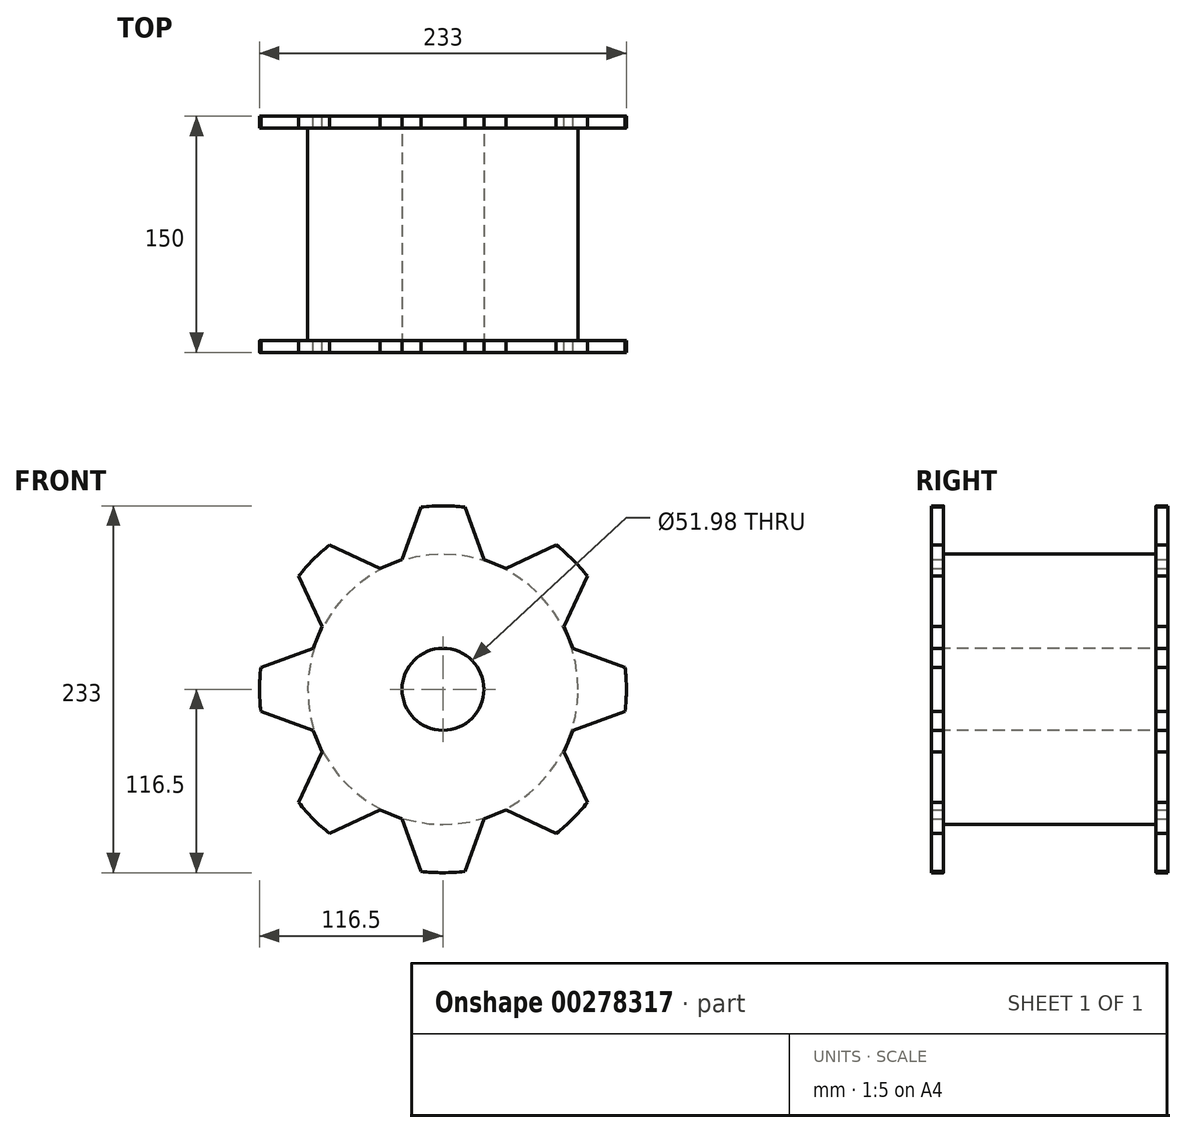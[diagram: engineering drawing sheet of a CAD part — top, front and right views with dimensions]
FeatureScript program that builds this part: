
annotation { "Feature Type Name" : "Feature", "Feature Type Description" : "" }
export const myFeature = defineFeature(function(context is Context, id is Id, definition is map)
    precondition{}
    {
        {
            var Q0;
            Q0=qCreatedBy(makeId("Front.planeOp"),FACE);
            var sketch = newSketch(context, id + "F0", { "sketchPlane" : qUnion([Q0])});
            skLineSegment(sketch, "E0", {"start": v(0, 0) * mm, "end": v(0, 116.5) * mm, "construction": true});
            skLineSegment(sketch, "E1", {"start": v(13.96, 115.66) * mm, "end": v(26.04, 82.49) * mm});
            skLineSegment(sketch, "E2", {"start": v(-13.96, 115.66) * mm, "end": v(-26.04, 82.49) * mm});
            skCircle(sketch, "E3", {"center": v(0, 0) * mm, "radius": 101.5 * mm, "construction": true});
            skArc(sketch, "E4", {"start": v(26.04, 82.49) * mm, "mid": v(0, 86.5) * mm, "end": v(-26.04, 82.49) * mm, "construction": true});
            skArc(sketch, "E5", {"start": v(13.96, 115.66) * mm, "mid": v(0, 116.5) * mm, "end": v(-13.96, 115.66) * mm});
            skPoint(sketch, "E6.startSnap0", {"position": v(-20, 99.07) * mm});
            skLineSegment(sketch, "E7", {"start": v(-20, 99.07) * mm, "end": v(20, 99.07) * mm});
            skArc(sketch, "E8.1.0", {"start": v(-71.91, 91.66) * mm, "mid": v(-82.38, 82.38) * mm, "end": v(-91.66, 71.91) * mm});
            skLineSegment(sketch, "E8.1.1", {"start": v(-71.91, 91.66) * mm, "end": v(-39.92, 76.74) * mm});
            skLineSegment(sketch, "E8.1.2", {"start": v(-91.66, 71.91) * mm, "end": v(-76.74, 39.92) * mm});
            skArc(sketch, "E8.2.0", {"start": v(-115.66, 13.96) * mm, "mid": v(-116.5, 0) * mm, "end": v(-115.66, -13.96) * mm});
            skLineSegment(sketch, "E8.2.1", {"start": v(-115.66, 13.96) * mm, "end": v(-82.49, 26.04) * mm});
            skLineSegment(sketch, "E8.2.2", {"start": v(-115.66, -13.96) * mm, "end": v(-82.49, -26.04) * mm});
            skArc(sketch, "E9.3.3.0", {"start": v(-91.66, -71.91) * mm, "mid": v(-82.38, -82.38) * mm, "end": v(-71.91, -91.66) * mm});
            skLineSegment(sketch, "E9.4.3.0", {"start": v(-91.66, -71.91) * mm, "end": v(-76.74, -39.92) * mm});
            skLineSegment(sketch, "E9.7.3.0", {"start": v(-71.91, -91.66) * mm, "end": v(-39.92, -76.74) * mm});
            skArc(sketch, "E10.3.4.0", {"start": v(-13.96, -115.66) * mm, "mid": v(0, -116.5) * mm, "end": v(13.96, -115.66) * mm});
            skLineSegment(sketch, "E10.4.4.0", {"start": v(-13.96, -115.66) * mm, "end": v(-26.04, -82.49) * mm});
            skLineSegment(sketch, "E10.7.4.0", {"start": v(13.96, -115.66) * mm, "end": v(26.04, -82.49) * mm});
            skArc(sketch, "E10.3.5.0", {"start": v(71.91, -91.66) * mm, "mid": v(82.38, -82.38) * mm, "end": v(91.66, -71.91) * mm});
            skLineSegment(sketch, "E10.4.5.0", {"start": v(71.91, -91.66) * mm, "end": v(39.92, -76.74) * mm});
            skLineSegment(sketch, "E10.7.5.0", {"start": v(91.66, -71.91) * mm, "end": v(76.74, -39.92) * mm});
            skArc(sketch, "E10.3.6.0", {"start": v(115.66, -13.96) * mm, "mid": v(116.5, 0) * mm, "end": v(115.66, 13.96) * mm});
            skLineSegment(sketch, "E10.4.6.0", {"start": v(115.66, -13.96) * mm, "end": v(82.49, -26.04) * mm});
            skLineSegment(sketch, "E10.7.6.0", {"start": v(115.66, 13.96) * mm, "end": v(82.49, 26.04) * mm});
            skArc(sketch, "E10.3.7.0", {"start": v(91.66, 71.91) * mm, "mid": v(82.38, 82.38) * mm, "end": v(71.91, 91.66) * mm});
            skLineSegment(sketch, "E10.4.7.0", {"start": v(91.66, 71.91) * mm, "end": v(76.74, 39.92) * mm});
            skLineSegment(sketch, "E10.7.7.0", {"start": v(71.91, 91.66) * mm, "end": v(39.92, 76.74) * mm});
            skLineSegment(sketch, "E11", {"start": v(-26.04, 82.49) * mm, "end": v(-39.92, 76.74) * mm});
            skLineSegment(sketch, "E12", {"start": v(-76.74, 39.92) * mm, "end": v(-82.49, 26.04) * mm});
            skLineSegment(sketch, "E13", {"start": v(-82.49, -26.04) * mm, "end": v(-76.74, -39.92) * mm});
            skLineSegment(sketch, "E14", {"start": v(-39.92, -76.74) * mm, "end": v(-26.04, -82.49) * mm});
            skLineSegment(sketch, "E15", {"start": v(26.04, -82.49) * mm, "end": v(39.92, -76.74) * mm});
            skLineSegment(sketch, "E16", {"start": v(76.74, -39.92) * mm, "end": v(82.49, -26.04) * mm});
            skLineSegment(sketch, "E17", {"start": v(82.49, 26.04) * mm, "end": v(76.74, 39.92) * mm});
            skLineSegment(sketch, "E18", {"start": v(39.92, 76.74) * mm, "end": v(26.04, 82.49) * mm});
            skSolve(sketch);
        }
        {
            var Q0;
            {var subQ0=sQuery(id+"F0.wireOp",EDGE,"E7");Q0=makeQuery(id+"F0.imprint","IMPRINT",FACE,{"disambiguationData":[TD([[makeQuery(id+"F0.imprint","IMPRINT",EDGE,{"derivedFrom":subQ0}),-1.0]])]});}
            var Q1;
            {var subQ0=sQuery(id+"F0.wireOp",EDGE,"E5");Q1=makeQuery(id+"F0.imprint","IMPRINT",FACE,{"disambiguationData":[TD([[makeQuery(id+"F0.imprint","IMPRINT",EDGE,{"derivedFrom":subQ0}),1.0]])]});}
            extrude(context, id + "F1", {"entities" : qUnion([Q0, Q1]), "depth" : 150 * mm});
        }
        {
            var Q0;
            Q0=qCreatedBy(makeId("Top.planeOp"),FACE);
            var sketch = newSketch(context, id + "F2", { "sketchPlane" : qUnion([Q0])});
            skLineSegment(sketch, "E19.bottom", {"start": v(-145.81, -142.5) * mm, "end": v(-85.81, -142.5) * mm});
            skLineSegment(sketch, "E19.top", {"start": v(-145.81, -7.5) * mm, "end": v(-85.81, -7.5) * mm});
            skLineSegment(sketch, "E19.left", {"start": v(-145.81, -142.5) * mm, "end": v(-145.81, -7.5) * mm});
            skLineSegment(sketch, "E19.right", {"start": v(-85.81, -142.5) * mm, "end": v(-85.81, -7.5) * mm});
            skLineSegment(sketch, "E20", {"start": v(0, 0) * mm, "end": v(0, -159.11) * mm, "construction": true});
            skSolve(sketch);
        }
        {
            var Q0;
            Q0 = qSketchRegion(id + "F2", true);
            var Q1;
            Q1=sQuery(id+"F2.wireOp",EDGE,"E20");
            revolve(context, id + "F3", {"operationType" : NewBodyOperationType.REMOVE, "entities" : qUnion([Q0]), "axis" : qUnion([Q1]), "revolveType" : RevolveType.FULL, "oppositeDirection" : true});
        }
        {
            var Q0;
            Q0=makeQuery(id+"F1.opExtrude","CAP_FACE",FACE,{"disambiguationData":[OSD([sQuery(id+"F0.wireOp",EDGE,"E1"),sQuery(id+"F0.wireOp",EDGE,"E2"),sQuery(id+"F0.wireOp",EDGE,"E5"),sQuery(id+"F0.wireOp",EDGE,"E8.1.0"),sQuery(id+"F0.wireOp",EDGE,"E8.1.1"),sQuery(id+"F0.wireOp",EDGE,"E8.1.2"),sQuery(id+"F0.wireOp",EDGE,"E8.2.0"),sQuery(id+"F0.wireOp",EDGE,"E8.2.1"),sQuery(id+"F0.wireOp",EDGE,"E8.2.2"),sQuery(id+"F0.wireOp",EDGE,"E9.3.3.0"),sQuery(id+"F0.wireOp",EDGE,"E9.4.3.0"),sQuery(id+"F0.wireOp",EDGE,"E9.7.3.0"),sQuery(id+"F0.wireOp",EDGE,"E10.3.4.0"),sQuery(id+"F0.wireOp",EDGE,"E10.4.4.0"),sQuery(id+"F0.wireOp",EDGE,"E10.7.4.0"),sQuery(id+"F0.wireOp",EDGE,"E10.3.5.0"),sQuery(id+"F0.wireOp",EDGE,"E10.4.5.0"),sQuery(id+"F0.wireOp",EDGE,"E10.7.5.0"),sQuery(id+"F0.wireOp",EDGE,"E10.3.6.0"),sQuery(id+"F0.wireOp",EDGE,"E10.4.6.0"),sQuery(id+"F0.wireOp",EDGE,"E10.7.6.0"),sQuery(id+"F0.wireOp",EDGE,"E10.3.7.0"),sQuery(id+"F0.wireOp",EDGE,"E10.4.7.0"),sQuery(id+"F0.wireOp",EDGE,"E10.7.7.0"),sQuery(id+"F0.wireOp",EDGE,"E11"),sQuery(id+"F0.wireOp",EDGE,"E12"),sQuery(id+"F0.wireOp",EDGE,"E13"),sQuery(id+"F0.wireOp",EDGE,"E14"),sQuery(id+"F0.wireOp",EDGE,"E15"),sQuery(id+"F0.wireOp",EDGE,"E16"),sQuery(id+"F0.wireOp",EDGE,"E17"),sQuery(id+"F0.wireOp",EDGE,"E18")])],"isStart":false});
            var sketch = newSketch(context, id + "F4", { "sketchPlane" : qUnion([Q0])});
            skCircle(sketch, "E21", {"center": v(0, 0) * mm, "radius": 26 * mm});
            skSolve(sketch);
        }
        {
            var Q0;
            Q0=makeQuery(id+"F4.imprint","IMPRINT",FACE,{"disambiguationData":[TD([[makeQuery(id+"F4.imprint","IMPRINT",EDGE,{"derivedFrom":sQuery(id+"F4.wireOp",EDGE,"E21")}),1.0]])]});
            extrude(context, id + "F5", {"entities" : qUnion([Q0]), "operationType" : NewBodyOperationType.REMOVE, "endBound" : BoundingType.THROUGH_ALL, "oppositeDirection" : true, "depth" : 25 * mm});
        }
    });
